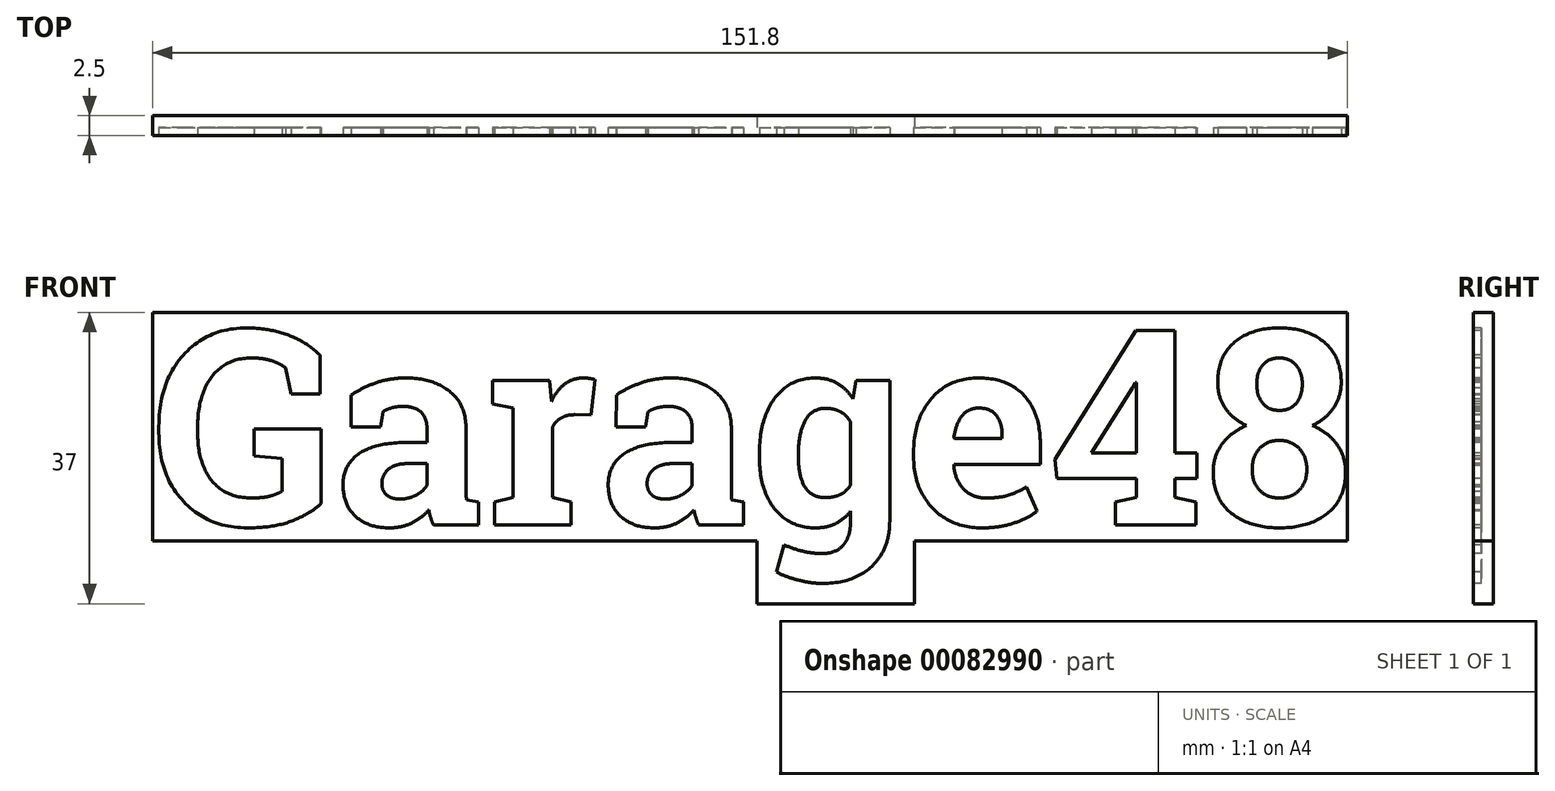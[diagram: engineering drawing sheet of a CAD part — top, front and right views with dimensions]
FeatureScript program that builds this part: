
annotation { "Feature Type Name" : "Feature", "Feature Type Description" : "" }
export const myFeature = defineFeature(function(context is Context, id is Id, definition is map)
    precondition{}
    {
        {
            var Q0;
            Q0=qCreatedBy(makeId("Front.planeOp"),FACE);
            var sketch = newSketch(context, id + "F0", { "sketchPlane" : qUnion([Q0])});
            skText(sketch, "E0", { "text": "Garage48", "fontName": "RobotoSlab-Bold.ttf"});
            skLineSegment(sketch, "E1.bottom", {"start": v(0, 27) * mm, "end": v(151.8, 27) * mm});
            skLineSegment(sketch, "E1.top", {"start": v(0, -2) * mm, "end": v(151.8, -2) * mm});
            skLineSegment(sketch, "E1.left", {"start": v(0, 27) * mm, "end": v(0, -2) * mm});
            skLineSegment(sketch, "E1.right", {"start": v(151.8, 27) * mm, "end": v(151.8, -2) * mm});
            skLineSegment(sketch, "E2.bottom", {"start": v(76.8, -2) * mm, "end": v(96.8, -2) * mm});
            skLineSegment(sketch, "E2.top", {"start": v(76.8, -10) * mm, "end": v(96.8, -10) * mm});
            skLineSegment(sketch, "E2.left", {"start": v(76.8, -2) * mm, "end": v(76.8, -10) * mm});
            skLineSegment(sketch, "E2.right", {"start": v(96.8, -2) * mm, "end": v(96.8, -10) * mm});
            const initialGuessF0  = {"E0": [0, 0, 1, 0, 0.025]};
            skSetInitialGuess(sketch, initialGuessF0);
            skSolve(sketch);
        }
        {
            var Q0;
            {var subQ0=sQuery(id+"F0.wireOp",EDGE,"E0.sketch_text.stroke-123");Q0=makeQuery(id+"F0.imprint","IMPRINT",FACE,{"disambiguationData":[TD([[makeQuery(id+"F0.imprint","IMPRINT",EDGE,{"derivedFrom":subQ0}),-1.0]])]});}
            var Q1;
            {var subQ9=sQuery(id+"F0.wireOp",EDGE,"E0.sketch_text.stroke-123");Q1=makeQuery(id+"F0.imprint","IMPRINT",FACE,{"disambiguationData":[TD([[makeQuery(id+"F0.imprint","IMPRINT",EDGE,{"derivedFrom":subQ9}),1.0]])]});}
            var Q2;
            Q2=makeQuery(id+"F0.imprint","IMPRINT",FACE,{"disambiguationData":[TD([[makeQuery(id+"F0.imprint","IMPRINT",EDGE,{"derivedFrom":sQuery(id+"F0.wireOp",EDGE,"E0.sketch_text.stroke-80")}),-1.0]])]});
            var Q3;
            Q3=makeQuery(id+"F0.imprint","IMPRINT",FACE,{"disambiguationData":[TD([[makeQuery(id+"F0.imprint","IMPRINT",EDGE,{"derivedFrom":sQuery(id+"F0.wireOp",EDGE,"E0.sketch_text.stroke-26")}),-1.0]])]});
            var Q4;
            Q4=makeQuery(id+"F0.imprint","IMPRINT",FACE,{"disambiguationData":[TD([[makeQuery(id+"F0.imprint","IMPRINT",EDGE,{"derivedFrom":sQuery(id+"F0.wireOp",EDGE,"E0.sketch_text.stroke-207")}),1.0]])]});
            var Q5;
            Q5=makeQuery(id+"F0.imprint","IMPRINT",FACE,{"disambiguationData":[TD([[makeQuery(id+"F0.imprint","IMPRINT",EDGE,{"derivedFrom":sQuery(id+"F0.wireOp",EDGE,"E0.sketch_text.stroke-164")}),1.0]])]});
            var Q6;
            Q6=makeQuery(id+"F0.imprint","IMPRINT",FACE,{"disambiguationData":[TD([[makeQuery(id+"F0.imprint","IMPRINT",EDGE,{"derivedFrom":sQuery(id+"F0.wireOp",EDGE,"E0.sketch_text.stroke-137")}),1.0]])]});
            var Q7;
            Q7=makeQuery(id+"F0.imprint","IMPRINT",FACE,{"disambiguationData":[TD([[makeQuery(id+"F0.imprint","IMPRINT",EDGE,{"derivedFrom":sQuery(id+"F0.wireOp",EDGE,"E0.sketch_text.stroke-107")}),1.0]])]});
            var Q8;
            Q8=makeQuery(id+"F0.imprint","IMPRINT",FACE,{"disambiguationData":[TD([[makeQuery(id+"F0.imprint","IMPRINT",EDGE,{"derivedFrom":sQuery(id+"F0.wireOp",EDGE,"E0.sketch_text.stroke-61")}),-1.0]])]});
            var Q9;
            Q9=makeQuery(id+"F0.imprint","IMPRINT",FACE,{"disambiguationData":[TD([[makeQuery(id+"F0.imprint","IMPRINT",EDGE,{"derivedFrom":sQuery(id+"F0.wireOp",EDGE,"E0.sketch_text.stroke-53")}),1.0]])]});
            var Q10;
            Q10=makeQuery(id+"F0.imprint","IMPRINT",FACE,{"disambiguationData":[TD([[makeQuery(id+"F0.imprint","IMPRINT",EDGE,{"derivedFrom":sQuery(id+"F0.wireOp",EDGE,"E0.sketch_text.stroke-0")}),-1.0]])]});
            var Q11;
            Q11=makeQuery(id+"F0.imprint","IMPRINT",FACE,{"disambiguationData":[TD([[makeQuery(id+"F0.imprint","IMPRINT",EDGE,{"derivedFrom":sQuery(id+"F0.wireOp",EDGE,"E0.sketch_text.stroke-147")}),-1.0]])]});
            var Q12;
            Q12=makeQuery(id+"F0.imprint","IMPRINT",FACE,{"disambiguationData":[TD([[makeQuery(id+"F0.imprint","IMPRINT",EDGE,{"derivedFrom":sQuery(id+"F0.wireOp",EDGE,"E0.sketch_text.stroke-115")}),-1.0]])]});
            var Q13;
            Q13=makeQuery(id+"F0.imprint","IMPRINT",FACE,{"disambiguationData":[TD([[makeQuery(id+"F0.imprint","IMPRINT",EDGE,{"derivedFrom":sQuery(id+"F0.wireOp",EDGE,"E0.sketch_text.stroke-191")}),-1.0]])]});
            var Q14;
            Q14=makeQuery(id+"F0.imprint","IMPRINT",FACE,{"disambiguationData":[TD([[makeQuery(id+"F0.imprint","IMPRINT",EDGE,{"derivedFrom":sQuery(id+"F0.wireOp",EDGE,"E0.sketch_text.stroke-0")}),1.0]])]});
            var Q15;
            Q15 = qSketchRegion(id + "F0", true);
            var Q16;
            Q16=makeQuery(id+"F0.imprint","IMPRINT",FACE,{"disambiguationData":[TD([[makeQuery(id+"F0.imprint","IMPRINT",EDGE,{"derivedFrom":sQuery(id+"F0.wireOp",EDGE,"E0.sketch_text.stroke-215")}),1.0]])]});
            var Q17;
            Q17=makeQuery(id+"F0.imprint","IMPRINT",FACE,{"disambiguationData":[TD([[makeQuery(id+"F0.imprint","IMPRINT",EDGE,{"derivedFrom":sQuery(id+"F0.wireOp",EDGE,"E0.sketch_text.stroke-186")}),1.0]])]});
            var Q18;
            Q18=makeQuery(id+"F0.imprint","IMPRINT",FACE,{"disambiguationData":[TD([[makeQuery(id+"F0.imprint","IMPRINT",EDGE,{"derivedFrom":sQuery(id+"F0.wireOp",EDGE,"E0.sketch_text.stroke-171")}),-1.0]])]});
            extrude(context, id + "F1", {"entities" : qUnion([Q0, Q1, Q2, Q3, Q4, Q5, Q6, Q7, Q8, Q9, Q10, Q11, Q12, Q13, Q14, Q15, Q16, Q17, Q18]), "oppositeDirection" : true, "depth" : 2.5 * mm});
        }
        {
            var Q0;
            Q0=makeQuery(id+"F0.imprint","IMPRINT",FACE,{"disambiguationData":[TD([[makeQuery(id+"F0.imprint","IMPRINT",EDGE,{"derivedFrom":sQuery(id+"F0.wireOp",EDGE,"E0.sketch_text.stroke-0")}),-1.0]])]});
            var Q1;
            Q1=makeQuery(id+"F0.imprint","IMPRINT",FACE,{"disambiguationData":[TD([[makeQuery(id+"F0.imprint","IMPRINT",EDGE,{"derivedFrom":sQuery(id+"F0.wireOp",EDGE,"E0.sketch_text.stroke-26")}),-1.0]])]});
            var Q2;
            Q2=makeQuery(id+"F0.imprint","IMPRINT",FACE,{"disambiguationData":[TD([[makeQuery(id+"F0.imprint","IMPRINT",EDGE,{"derivedFrom":sQuery(id+"F0.wireOp",EDGE,"E0.sketch_text.stroke-61")}),-1.0]])]});
            var Q3;
            Q3=makeQuery(id+"F0.imprint","IMPRINT",FACE,{"disambiguationData":[TD([[makeQuery(id+"F0.imprint","IMPRINT",EDGE,{"derivedFrom":sQuery(id+"F0.wireOp",EDGE,"E0.sketch_text.stroke-80")}),-1.0]])]});
            var Q4;
            Q4=makeQuery(id+"F0.imprint","IMPRINT",FACE,{"disambiguationData":[TD([[makeQuery(id+"F0.imprint","IMPRINT",EDGE,{"derivedFrom":sQuery(id+"F0.wireOp",EDGE,"E0.sketch_text.stroke-115")}),-1.0]])]});
            var Q5;
            Q5=makeQuery(id+"F0.imprint","IMPRINT",FACE,{"disambiguationData":[TD([[makeQuery(id+"F0.imprint","IMPRINT",EDGE,{"derivedFrom":sQuery(id+"F0.wireOp",EDGE,"E0.sketch_text.stroke-147")}),-1.0]])]});
            var Q6;
            {var subQ0=sQuery(id+"F0.wireOp",EDGE,"E0.sketch_text.stroke-123");Q6=makeQuery(id+"F0.imprint","IMPRINT",FACE,{"disambiguationData":[TD([[makeQuery(id+"F0.imprint","IMPRINT",EDGE,{"derivedFrom":subQ0}),-1.0]])]});}
            extrude(context, id + "F2", {"entities" : qUnion([Q0, Q1, Q2, Q3, Q4, Q5, Q6]), "operationType" : NewBodyOperationType.REMOVE, "oppositeDirection" : true, "depth" : 1 * mm});
        }
        {
            var Q0;
            Q0=makeQuery(id+"F0.imprint","IMPRINT",FACE,{"disambiguationData":[TD([[makeQuery(id+"F0.imprint","IMPRINT",EDGE,{"derivedFrom":sQuery(id+"F0.wireOp",EDGE,"E0.sketch_text.stroke-191")}),-1.0]])]});
            var Q1;
            Q1=makeQuery(id+"F0.imprint","IMPRINT",FACE,{"disambiguationData":[TD([[makeQuery(id+"F0.imprint","IMPRINT",EDGE,{"derivedFrom":sQuery(id+"F0.wireOp",EDGE,"E0.sketch_text.stroke-171")}),-1.0]])]});
            extrude(context, id + "F3", {"entities" : qUnion([Q0, Q1]), "oppositeDirection" : true, "depth" : 1 * mm});
        }
        {
            var Q0;
            Q0=makeQuery(id+"F3.opExtrude","SWEPT_BODY",BODY,{"disambiguationData":[OSD([sQuery(id+"F0.wireOp",EDGE,"E0.sketch_text.stroke-171"),sQuery(id+"F0.wireOp",EDGE,"E0.sketch_text.stroke-172"),sQuery(id+"F0.wireOp",EDGE,"E0.sketch_text.stroke-173"),sQuery(id+"F0.wireOp",EDGE,"E0.sketch_text.stroke-174"),sQuery(id+"F0.wireOp",EDGE,"E0.sketch_text.stroke-175"),sQuery(id+"F0.wireOp",EDGE,"E0.sketch_text.stroke-176"),sQuery(id+"F0.wireOp",EDGE,"E0.sketch_text.stroke-177"),sQuery(id+"F0.wireOp",EDGE,"E0.sketch_text.stroke-178"),sQuery(id+"F0.wireOp",EDGE,"E0.sketch_text.stroke-179"),sQuery(id+"F0.wireOp",EDGE,"E0.sketch_text.stroke-180"),sQuery(id+"F0.wireOp",EDGE,"E0.sketch_text.stroke-181"),sQuery(id+"F0.wireOp",EDGE,"E0.sketch_text.stroke-182"),sQuery(id+"F0.wireOp",EDGE,"E0.sketch_text.stroke-183"),sQuery(id+"F0.wireOp",EDGE,"E0.sketch_text.stroke-184"),sQuery(id+"F0.wireOp",EDGE,"E0.sketch_text.stroke-185"),sQuery(id+"F0.wireOp",EDGE,"E0.sketch_text.stroke-186"),sQuery(id+"F0.wireOp",EDGE,"E0.sketch_text.stroke-187"),sQuery(id+"F0.wireOp",EDGE,"E0.sketch_text.stroke-188"),sQuery(id+"F0.wireOp",EDGE,"E0.sketch_text.stroke-189"),sQuery(id+"F0.wireOp",EDGE,"E0.sketch_text.stroke-190")])]});
            var Q1;
            Q1=makeQuery(id+"F3.opExtrude","SWEPT_BODY",BODY,{"disambiguationData":[OSD([sQuery(id+"F0.wireOp",EDGE,"E0.sketch_text.stroke-191"),sQuery(id+"F0.wireOp",EDGE,"E0.sketch_text.stroke-192"),sQuery(id+"F0.wireOp",EDGE,"E0.sketch_text.stroke-193"),sQuery(id+"F0.wireOp",EDGE,"E0.sketch_text.stroke-194"),sQuery(id+"F0.wireOp",EDGE,"E0.sketch_text.stroke-195"),sQuery(id+"F0.wireOp",EDGE,"E0.sketch_text.stroke-196"),sQuery(id+"F0.wireOp",EDGE,"E0.sketch_text.stroke-197"),sQuery(id+"F0.wireOp",EDGE,"E0.sketch_text.stroke-198"),sQuery(id+"F0.wireOp",EDGE,"E0.sketch_text.stroke-199"),sQuery(id+"F0.wireOp",EDGE,"E0.sketch_text.stroke-200"),sQuery(id+"F0.wireOp",EDGE,"E0.sketch_text.stroke-201"),sQuery(id+"F0.wireOp",EDGE,"E0.sketch_text.stroke-202"),sQuery(id+"F0.wireOp",EDGE,"E0.sketch_text.stroke-203"),sQuery(id+"F0.wireOp",EDGE,"E0.sketch_text.stroke-204"),sQuery(id+"F0.wireOp",EDGE,"E0.sketch_text.stroke-205"),sQuery(id+"F0.wireOp",EDGE,"E0.sketch_text.stroke-206"),sQuery(id+"F0.wireOp",EDGE,"E0.sketch_text.stroke-207"),sQuery(id+"F0.wireOp",EDGE,"E0.sketch_text.stroke-208"),sQuery(id+"F0.wireOp",EDGE,"E0.sketch_text.stroke-209"),sQuery(id+"F0.wireOp",EDGE,"E0.sketch_text.stroke-210"),sQuery(id+"F0.wireOp",EDGE,"E0.sketch_text.stroke-211"),sQuery(id+"F0.wireOp",EDGE,"E0.sketch_text.stroke-212"),sQuery(id+"F0.wireOp",EDGE,"E0.sketch_text.stroke-213"),sQuery(id+"F0.wireOp",EDGE,"E0.sketch_text.stroke-214"),sQuery(id+"F0.wireOp",EDGE,"E0.sketch_text.stroke-215"),sQuery(id+"F0.wireOp",EDGE,"E0.sketch_text.stroke-216"),sQuery(id+"F0.wireOp",EDGE,"E0.sketch_text.stroke-217"),sQuery(id+"F0.wireOp",EDGE,"E0.sketch_text.stroke-218"),sQuery(id+"F0.wireOp",EDGE,"E0.sketch_text.stroke-219"),sQuery(id+"F0.wireOp",EDGE,"E0.sketch_text.stroke-220"),sQuery(id+"F0.wireOp",EDGE,"E0.sketch_text.stroke-221"),sQuery(id+"F0.wireOp",EDGE,"E0.sketch_text.stroke-222")])]});
            var Q2;
            Q2=makeQuery(id+"F1.opExtrude","SWEPT_BODY",BODY,{"disambiguationData":[OSD([sQuery(id+"F0.wireOp",EDGE,"E1.bottom"),sQuery(id+"F0.wireOp",EDGE,"E1.top"),sQuery(id+"F0.wireOp",EDGE,"E1.left"),sQuery(id+"F0.wireOp",EDGE,"E1.right"),sQuery(id+"F0.wireOp",EDGE,"E2.top"),sQuery(id+"F0.wireOp",EDGE,"E2.left"),sQuery(id+"F0.wireOp",EDGE,"E2.right")])]});
            booleanBodies(context, id + "F4", {"operationType" : BooleanOperationType.SUBTRACTION, "tools" : qUnion([Q0, Q1]), "targets" : qUnion([Q2])});
        }
    });
